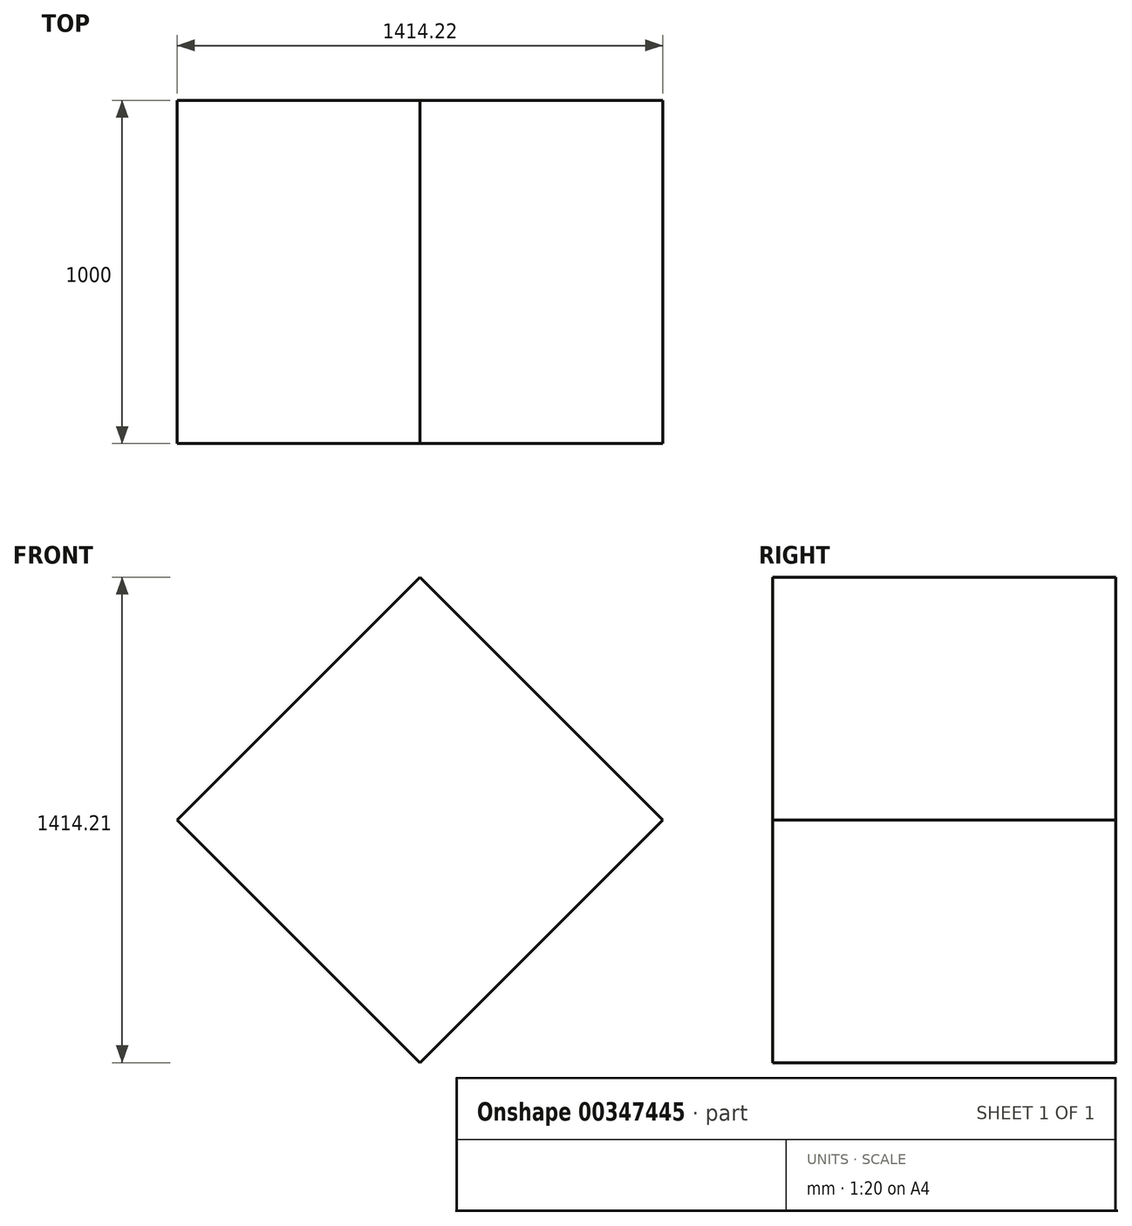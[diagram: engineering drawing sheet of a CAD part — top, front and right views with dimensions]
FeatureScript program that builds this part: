
annotation { "Feature Type Name" : "Feature", "Feature Type Description" : "" }
export const myFeature = defineFeature(function(context is Context, id is Id, definition is map)
    precondition{}
    {
        {
            var Q0;
            Q0=qCreatedBy(makeId("Front.planeOp"),FACE);
            var sketch = newSketch(context, id + "F0", { "sketchPlane" : qUnion([Q0])});
            skLineSegment(sketch, "E0.bottom", {"start": v(0, 0) * mm, "end": v(1000, 0) * mm});
            skLineSegment(sketch, "E0.top", {"start": v(0, 1000) * mm, "end": v(1000, 1000) * mm});
            skLineSegment(sketch, "E0.left", {"start": v(0, 0) * mm, "end": v(0, 1000) * mm});
            skLineSegment(sketch, "E0.right", {"start": v(1000, 0) * mm, "end": v(1000, 1000) * mm});
            skSolve(sketch);
        }
        {
            var Q0;
            Q0=makeQuery(id+"F0.imprint","IMPRINT",FACE,{"disambiguationData":[TD([[makeQuery(id+"F0.imprint","IMPRINT",EDGE,{"derivedFrom":sQuery(id+"F0.wireOp",EDGE,"E0.bottom")}),1.0]])]});
            extrude(context, id + "F1", {"entities" : qUnion([Q0]), "offsetDistance" : 25 * mm, "depth" : -1000 * mm});
        }
        {
            var Q0;
            Q0=makeQuery(id+"F1.opExtrude","SWEPT_BODY",BODY,{"disambiguationData":[OSD([sQuery(id+"F0.wireOp",EDGE,"E0.bottom"),sQuery(id+"F0.wireOp",EDGE,"E0.top"),sQuery(id+"F0.wireOp",EDGE,"E0.left"),sQuery(id+"F0.wireOp",EDGE,"E0.right")])]});
            var Q1;
            Q1=makeQuery(id+"F1.opExtrude","SWEPT_EDGE",EDGE,{"disambiguationData":[OSD([sQuery(id+"F0.wireOp",EDGE,"E0.bottom"),sQuery(id+"F0.wireOp",EDGE,"E0.left")])]});
            transform(context, id + "F2", {"entities" : qUnion([Q0]), "transformType" : TransformType.ROTATION, "transformAxis" : qUnion([Q1]), "angle" : 45 * degree, "makeCopy" : false});
        }
    });
